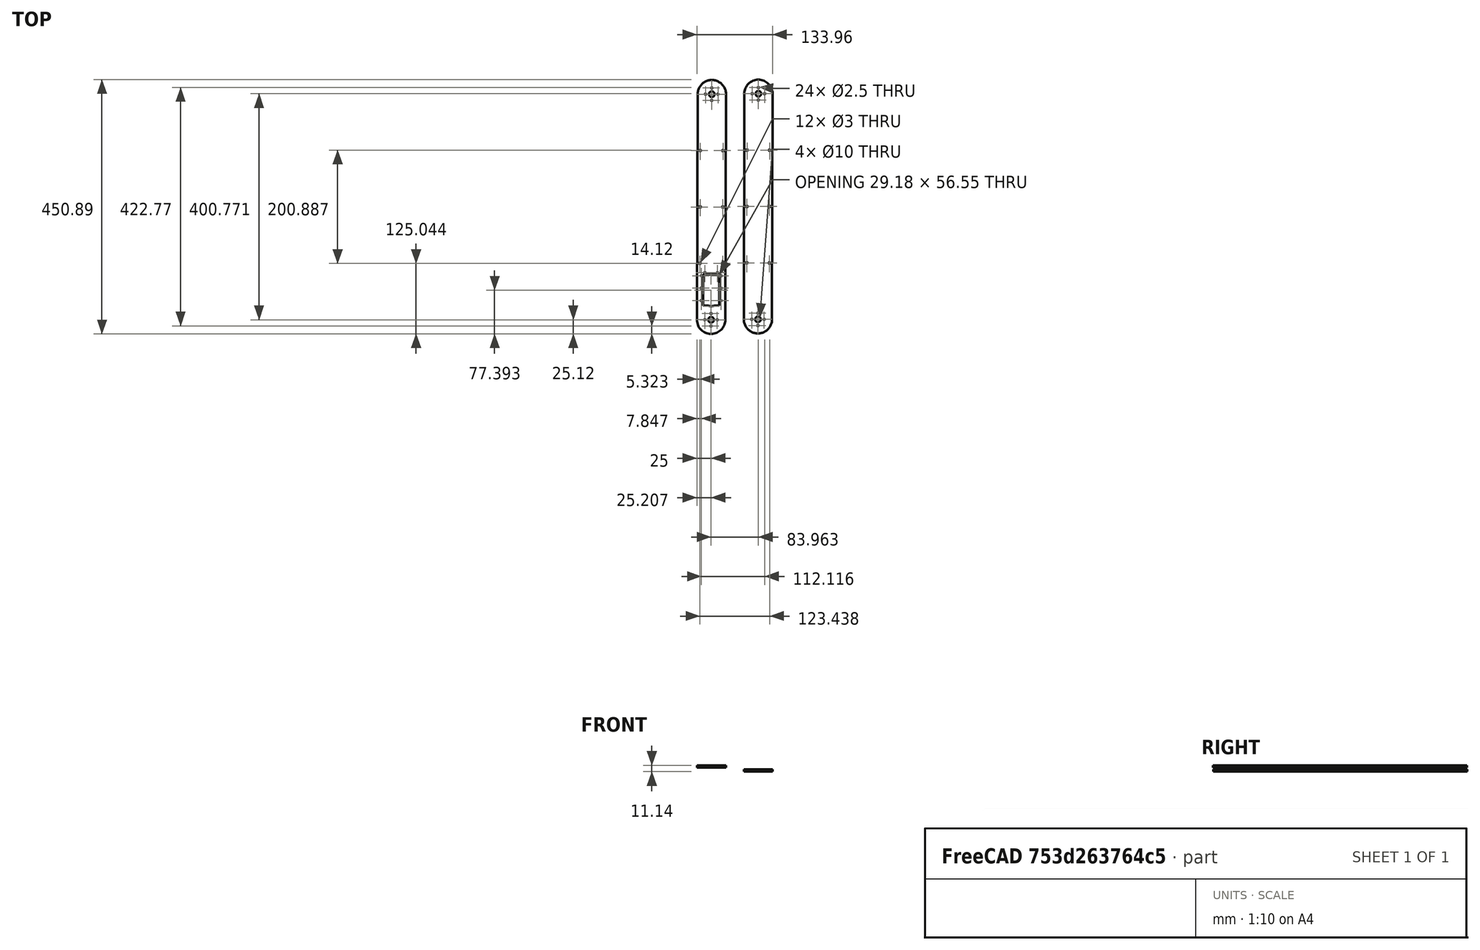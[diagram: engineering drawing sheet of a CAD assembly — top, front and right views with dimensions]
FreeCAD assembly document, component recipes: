
FREECAD ASSEMBLY — COMPONENT RECIPES ("arm_assembly2")

This assembly document has 4 components, labeled P0..P3 below (a component is one placed body or linked part). 2 of them carry a construction recipe — the FreeCAD feature program that regenerates the part from scratch, quoted from this document or its linked companion documents; the rest are supplied as boundary geometry only. No exploded tour is included for this assembly.
COMPONENT P0 — recipe-attached ("arm_low_1", modeled in this document).
Construction recipe (the document's own serialized feature program — sketch geometry with constraints, then the solid features built on it; lengths are millimeters unless a unit is written):

FEATURE [Sketcher::SketchObject] Sketch
  ArcFitTolerance = 1e-06
  AttachmentSupport = -> [XY_Plane]
  FullyConstrained = false
  MakeInternals = false
  MapMode = 5
  sketch-geometry (67):
    g0: LineSegment [constr] StartX=1.5008e-12 StartY=20 StartZ=0 EndX=1.5008e-12 EndY=-20 EndZ=0
    g1: LineSegment [constr] StartX=-2.359e-12 StartY=0 StartZ=0 EndX=-2.359e-12 EndY=400 EndZ=0
    g2: LineSegment [constr] StartX=1.5008e-12 StartY=20 StartZ=0 EndX=1.5008e-12 EndY=25 EndZ=0
    g3: Circle CenterX=-2.359e-12 CenterY=400 CenterZ=0 NormalX=0 NormalY=0 NormalZ=1 AngleXU=0 Radius=5
    g4: Circle CenterX=-2.359e-12 CenterY=400 CenterZ=0 NormalX=0 NormalY=0 NormalZ=1 AngleXU=0 Radius=2
    g5: Circle CenterX=-10.9997 CenterY=400 CenterZ=0 NormalX=0 NormalY=0 NormalZ=1 AngleXU=0 Radius=1.25
    g6: Circle CenterX=0 CenterY=389 CenterZ=0 NormalX=0 NormalY=0 NormalZ=1 AngleXU=0 Radius=1.25
    g7: Circle CenterX=10.9997 CenterY=400 CenterZ=0 NormalX=0 NormalY=0 NormalZ=1 AngleXU=0 Radius=1.25
    g8: Circle CenterX=0 CenterY=411 CenterZ=0 NormalX=0 NormalY=0 NormalZ=1 AngleXU=0 Radius=1.25
    g9: LineSegment [constr] StartX=0 StartY=-5 StartZ=0 EndX=0 EndY=5.99996 EndZ=0
    g10: Circle [constr] CenterX=0 CenterY=0 CenterZ=0 NormalX=0 NormalY=0 NormalZ=1 AngleXU=0 Radius=14
    g11: LineSegment [constr] StartX=0 StartY=0 StartZ=0 EndX=25.23 EndY=0 EndZ=0
    g12: Circle [constr] CenterX=0 CenterY=-3.8e-05 CenterZ=0 NormalX=0 NormalY=0 NormalZ=1 AngleXU=0 Radius=11
    g13: Circle CenterX=0 CenterY=0 CenterZ=0 NormalX=0 NormalY=0 NormalZ=1 AngleXU=0 Radius=5
    g14: Circle CenterX=10.9997 CenterY=0 CenterZ=0 NormalX=0 NormalY=0 NormalZ=1 AngleXU=0 Radius=1.25
    g15: Circle CenterX=-10.9997 CenterY=0 CenterZ=0 NormalX=0 NormalY=0 NormalZ=1 AngleXU=0 Radius=1.25
    g16: Circle CenterX=0 CenterY=-10.9997 CenterZ=0 NormalX=0 NormalY=0 NormalZ=1 AngleXU=0 Radius=1.25
    g17: Circle CenterX=0 CenterY=11 CenterZ=0 NormalX=0 NormalY=0 NormalZ=1 AngleXU=0 Radius=1.25
    g18: LineSegment [constr] StartX=0 StartY=0 StartZ=0 EndX=-25 EndY=0 EndZ=0
    g19: LineSegment [constr] StartX=20.1368 StartY=86.0999 StartZ=0 EndX=20.1368 EndY=24.9999 EndZ=0
    g20: LineSegment [constr] StartX=0.036848 StartY=80.5 StartZ=0 EndX=14.5368 EndY=80.5 EndZ=0
    g21: LineSegment StartX=14.5368 StartY=80.5 StartZ=0 EndX=-14.4632 EndY=80.5 EndZ=0
    g22: LineSegment StartX=14.5368 StartY=80.5 StartZ=0 EndX=14.5368 EndY=24.9999 EndZ=0
    g23: Circle CenterX=11.0368 CenterY=83.3 CenterZ=0 NormalX=0 NormalY=0 NormalZ=1 AngleXU=0 Radius=1.25
    g24: Circle CenterX=17.3368 CenterY=78 CenterZ=0 NormalX=0 NormalY=0 NormalZ=1 AngleXU=0 Radius=1.25
    g25: LineSegment [constr] StartX=-20.0632 StartY=86.0999 StartZ=0 EndX=20.1368 EndY=86.0999 EndZ=0
    g26: Circle CenterX=17.3368 CenterY=56 CenterZ=0 NormalX=0 NormalY=0 NormalZ=1 AngleXU=0 Radius=1.25
    g27: Circle CenterX=17.3368 CenterY=34 CenterZ=0 NormalX=0 NormalY=0 NormalZ=1 AngleXU=0 Radius=1.25
    g28: Circle [constr] CenterX=0.036848 CenterY=37.9999 CenterZ=0 NormalX=0 NormalY=0 NormalZ=1 AngleXU=0 Radius=14
    g29: ArcOfCircle CenterX=0.036848 CenterY=37.9999 CenterZ=0 NormalX=0 NormalY=0 NormalZ=1 AngleXU=0 Radius=14 StartAngle=4.33214 EndAngle=5.09264
    g30: LineSegment StartX=5.233 StartY=24.9999 StartZ=0 EndX=14.5368 EndY=24.9999 EndZ=0
    g31: LineSegment [constr] StartX=14.5368 StartY=24.9999 StartZ=0 EndX=20.1368 EndY=24.9999 EndZ=0
    g32: LineSegment [constr] StartX=17.3368 StartY=56 StartZ=0 EndX=-17.2632 EndY=56 EndZ=0
    g33: LineSegment [constr] StartX=-20.0632 StartY=24.9999 StartZ=0 EndX=-20.0632 EndY=86.0999 EndZ=0
    g34: LineSegment StartX=-14.4632 StartY=80.5 StartZ=0 EndX=-14.4632 EndY=24.9999 EndZ=0
    g35: Circle CenterX=-17.2632 CenterY=78 CenterZ=0 NormalX=0 NormalY=0 NormalZ=1 AngleXU=0 Radius=1.25
    g36: Circle CenterX=-10.9632 CenterY=83.3 CenterZ=0 NormalX=0 NormalY=0 NormalZ=1 AngleXU=0 Radius=1.25
    g37: Circle CenterX=-17.2632 CenterY=56 CenterZ=0 NormalX=0 NormalY=0 NormalZ=1 AngleXU=0 Radius=1.25
    g38: Circle CenterX=-17.2632 CenterY=34 CenterZ=0 NormalX=0 NormalY=0 NormalZ=1 AngleXU=0 Radius=1.25
    g39: LineSegment StartX=-14.4632 StartY=24.9999 StartZ=0 EndX=-5.15931 EndY=24.9999 EndZ=0
    g40: LineSegment [constr] StartX=-20.0632 StartY=24.9999 StartZ=0 EndX=-14.4632 EndY=24.9999 EndZ=0
    g41: ArcOfCircle CenterX=0.115002 CenterY=3.75548e-06 CenterZ=0 NormalX=0 NormalY=0 NormalZ=1 AngleXU=0 Radius=25.115 StartAngle=3.14159 EndAngle=6.28319
    g42: ArcOfCircle CenterX=0.115002 CenterY=399.959 CenterZ=0 NormalX=0 NormalY=0 NormalZ=1 AngleXU=0 Radius=25.115 StartAngle=0 EndAngle=3.14159
    g43: LineSegment StartX=-25 StartY=3.75548e-06 StartZ=0 EndX=-25 EndY=399.959 EndZ=0
    g44: LineSegment StartX=25.23 StartY=3.75548e-06 StartZ=0 EndX=25.23 EndY=399.959 EndZ=0
    g45: LineSegment [constr] StartX=25.23 StartY=199.98 StartZ=0 EndX=-25 EndY=199.98 EndZ=0
    g46: LineSegment [constr] StartX=25.23 StartY=199.98 StartZ=0 EndX=55.23 EndY=199.98 EndZ=0
    g47: LineSegment [constr] StartX=25.23 StartY=0 StartZ=0 EndX=55.23 EndY=0 EndZ=0
    g48: LineSegment [constr] StartX=55.23 StartY=0 StartZ=0 EndX=55.23 EndY=199.98 EndZ=0
    g49: LineSegment [constr] StartX=55.23 StartY=99.9898 StartZ=0 EndX=25.23 EndY=99.9898 EndZ=0
    g50: LineSegment [constr] StartX=25.23 StartY=99.9898 StartZ=0 EndX=-25 EndY=99.9898 EndZ=0
    g51: LineSegment [constr] StartX=25.23 StartY=399.959 StartZ=0 EndX=55.23 EndY=399.959 EndZ=0
    g52: LineSegment [constr] StartX=55.23 StartY=399.959 StartZ=0 EndX=55.23 EndY=199.98 EndZ=0
    g53: LineSegment [constr] StartX=55.23 StartY=299.969 StartZ=0 EndX=25.23 EndY=299.969 EndZ=0
    g54: LineSegment [constr] StartX=25.23 StartY=299.969 StartZ=0 EndX=-25 EndY=299.969 EndZ=0
    g55: LineSegment [constr] StartX=-25 StartY=299.969 StartZ=0 EndX=-20 EndY=299.969 EndZ=0
    g56: LineSegment [constr] StartX=-20 StartY=299.969 StartZ=0 EndX=-20 EndY=199.98 EndZ=0
    g57: LineSegment [constr] StartX=-20 StartY=199.98 StartZ=0 EndX=-20 EndY=99.9898 EndZ=0
    g58: LineSegment [constr] StartX=25.23 StartY=299.969 StartZ=0 EndX=20.23 EndY=299.969 EndZ=0
    g59: LineSegment [constr] StartX=20.23 StartY=299.969 StartZ=0 EndX=20.23 EndY=199.98 EndZ=0
    g60: LineSegment [constr] StartX=20.23 StartY=199.98 StartZ=0 EndX=20.23 EndY=99.9898 EndZ=0
    g61: Circle CenterX=-20 CenterY=299.969 CenterZ=0 NormalX=0 NormalY=0 NormalZ=1 AngleXU=0 Radius=1.5
    g62: Circle CenterX=20.23 CenterY=299.969 CenterZ=0 NormalX=0 NormalY=0 NormalZ=1 AngleXU=0 Radius=1.5
    g63: Circle CenterX=-20 CenterY=199.98 CenterZ=0 NormalX=0 NormalY=0 NormalZ=1 AngleXU=0 Radius=1.5
    g64: Circle CenterX=20.23 CenterY=199.98 CenterZ=0 NormalX=0 NormalY=0 NormalZ=1 AngleXU=0 Radius=1.5
    g65: Circle CenterX=-20 CenterY=99.9898 CenterZ=0 NormalX=0 NormalY=0 NormalZ=1 AngleXU=0 Radius=1.5
    g66: Circle CenterX=20.23 CenterY=99.9898 CenterZ=0 NormalX=0 NormalY=0 NormalZ=1 AngleXU=0 Radius=1.5
  constraints (132):
    c: Vertical(g0)
    c: Vertical(g1)
    c: Coincident(g2,g0)
    c: Vertical(g2)
    c: Diameter(g3) = 10
    c: Coincident(g3,g1)
    c: Diameter(g4) = 4
    c: Coincident(g4,g1)
    c: Diameter(g8) = 2.5
    c: Diameter(g5) = 2.5
    c: Diameter(g6) = 2.5
    c: Diameter(g7) = 2.5
    c: Vertical(g9)
    c: Diameter(g10) = 28
    c: Coincident(g18,g10)
    c: Horizontal(g18)
    c: Coincident(g11,g10)
    c: Horizontal(g11)
    c: Diameter(g12) = 22
    c: Diameter(g13) = 10
    c: Coincident(g13,g10)
    c: Diameter(g17) = 2.5
    c: Diameter(g15) = 2.5
    c: Diameter(g16) = 2.5
    c: Diameter(g14) = 2.5
    c: Coincident(g25,g19)
    c: Coincident(g33,g25)
    c: Horizontal(g25)
    c: Vertical(g19)
    c: Vertical(g33)
    c: Distance(g19,g33) = 40.2
    c: Distance(g25,g33) = 61.1
    c: Diameter(g29) = 28
    c: Horizontal(g20)
    c: Coincident(g21,g20)
    c: Horizontal(g21)
    c: Coincident(g34,g21)
    c: Vertical(g34)
    c: Coincident(g22,g20)
    c: Vertical(g22)
    c: Diameter(g23) = 2.5
    c: Equal(g23,g36)
    c: Equal(g23,g27)
    c: Equal(g23,g38)
    c: Equal(g23,g37)
    c: Equal(g23,g35)
    c: Equal(g23,g24)
    c: Equal(g23,g26)
    c: Coincident(g28,g29)
    c: PointOnObject(g29,g28)
    c: Coincident(g30,g29)
    c: Coincident(g30,g22)
    c: Horizontal(g30)
    c: Coincident(g31,g22)
    c: Coincident(g31,g19)
    c: Horizontal(g31)
    c: Coincident(g39,g34)
    c: Coincident(g39,g29)
    c: Horizontal(g39)
    c: Coincident(g40,g33)
    c: Coincident(g40,g34)
    c: Horizontal(g40)
    c: Coincident(g32,g26)
    c: Coincident(g32,g37)
    c: Horizontal(g32)
    c: DistanceY(g28,g1) = 362
    c: Tangent(g41,g43) = 1.5708
    c: Tangent(g41,g44) = -1.5708
    c: Tangent(g42,g43) = 1.5708
    c: Tangent(g42,g44) = -1.5708
    c: Equal(g41,g42)
    c: Symmetric(g44,g44,g45)
    c: Symmetric(g43,g43,g45)
    c: Horizontal(g45)
    c: Distance(g46) = 30
    c: Horizontal(g46)
    c: Coincident(g46,g45)
    c: Distance(g47) = 30
    c: Horizontal(g47)
    c: Coincident(g47,g11)
    c: PointOnObject(g47,g-1)
    c: Coincident(g48,g47)
    c: Coincident(g48,g46)
    c: Vertical(g48)
    c: Symmetric(g48,g48,g49)
    c: PointOnObject(g49,g44)
    c: Horizontal(g49)
    c: Coincident(g50,g49)
    c: PointOnObject(g50,g43)
    c: Horizontal(g50)
    c: Distance(g51) = 30
    c: Horizontal(g51)
    c: Coincident(g51,g42)
    c: Coincident(g52,g51)
    c: Coincident(g52,g46)
    c: Symmetric(g52,g52,g53)
    c: PointOnObject(g53,g44)
    c: Horizontal(g53)
    c: Coincident(g54,g53)
    c: PointOnObject(g54,g43)
    c: Horizontal(g54)
    c: Distance(g55) = 5
    c: Coincident(g55,g54)
    c: PointOnObject(g55,g54)
    c: Coincident(g56,g55)
    c: PointOnObject(g56,g45)
    c: Vertical(g56)
    c: Coincident(g57,g56)
    c: PointOnObject(g57,g50)
    c: Vertical(g57)
    c: Distance(g58) = 5
    c: Coincident(g58,g53)
    c: PointOnObject(g58,g54)
    c: Coincident(g59,g58)
    c: PointOnObject(g59,g45)
    c: Vertical(g59)
    c: Coincident(g60,g59)
    c: PointOnObject(g60,g50)
    c: Vertical(g60)
    c: Coincident(g61,g55)
    c: Diameter(g61) = 3
    c: Coincident(g62,g58)
    c: Equal(g61,g62)
    c: Coincident(g63,g56)
    c: Equal(g61,g63)
    c: Coincident(g64,g59)
    c: Equal(g63,g64)
    c: Coincident(g65,g57)
    c: Equal(g63,g65)
    c: Coincident(g66,g60)
    c: Equal(g65,g66)
    c: DistanceY(g41,g28) = 37.9999
FEATURE [PartDesign::Pad] Pad
  Direction = (0,0,1)
  Length = 4
  Length2 = 10
  Profile = -> Sketch
  ReferenceAxis = -> Sketch [N_Axis]
  Refine = true
  Suppressed = false
  Type = 0
FEATURE [PartDesign::Body] Body  label="arm_low_1"
  AllowCompound = false
  Group = -> [Sketch,Pad]
  Origin = -> Origin
  Placement = pos=(0,0,25.3) rot=(0,0,-1;0.003227rad)
  Tip = -> Pad
COMPONENT P1 — recipe-attached ("arm_high_1", modeled in this document).
Construction recipe (the document's own serialized feature program — sketch geometry with constraints, then the solid features built on it; lengths are millimeters unless a unit is written):

FEATURE [Sketcher::SketchObject] Sketch001
  ArcFitTolerance = 1e-06
  FullyConstrained = false
  MakeInternals = false
  MapMode = 5
  sketch-geometry (41):
    g0: Circle [constr] CenterX=7e-16 CenterY=0.000303 CenterZ=0 NormalX=0 NormalY=0 NormalZ=1 AngleXU=0 Radius=14
    g1: LineSegment [constr] StartX=7e-16 StartY=0.000303 StartZ=0 EndX=7e-16 EndY=400.001 EndZ=0
    g2: Circle CenterX=7e-16 CenterY=400.001 CenterZ=0 NormalX=0 NormalY=0 NormalZ=1 AngleXU=0 Radius=5
    g3: Circle CenterX=7e-16 CenterY=0 CenterZ=0 NormalX=0 NormalY=0 NormalZ=1 AngleXU=0 Radius=5
    g4: Circle CenterX=7e-16 CenterY=400.001 CenterZ=0 NormalX=0 NormalY=0 NormalZ=1 AngleXU=0 Radius=2
    g5: Circle CenterX=7e-16 CenterY=0.000303 CenterZ=0 NormalX=0 NormalY=0 NormalZ=1 AngleXU=0 Radius=2
    g6: Circle [constr] CenterX=0 CenterY=0 CenterZ=0 NormalX=0 NormalY=0 NormalZ=1 AngleXU=0 Radius=11
    g7: ArcOfCircle CenterX=7e-16 CenterY=0 CenterZ=0 NormalX=0 NormalY=0 NormalZ=1 AngleXU=0 Radius=25 StartAngle=3.14159 EndAngle=6.28319
    g8: ArcOfCircle CenterX=7e-16 CenterY=400.001 CenterZ=0 NormalX=0 NormalY=0 NormalZ=1 AngleXU=0 Radius=25 StartAngle=6e-16 EndAngle=3.14159
    g9: LineSegment StartX=-25 StartY=-8e-15 StartZ=0 EndX=-25 EndY=400.001 EndZ=0
    g10: LineSegment StartX=25 StartY=0 StartZ=0 EndX=25 EndY=400.001 EndZ=0
    g11: Circle CenterX=10.9997 CenterY=400.001 CenterZ=0 NormalX=0 NormalY=0 NormalZ=1 AngleXU=0 Radius=1.25
    g12: Circle CenterX=0 CenterY=411.001 CenterZ=0 NormalX=0 NormalY=0 NormalZ=1 AngleXU=0 Radius=1.25
    g13: Circle CenterX=-10.9997 CenterY=400.001 CenterZ=0 NormalX=0 NormalY=0 NormalZ=1 AngleXU=0 Radius=1.25
    g14: Circle CenterX=0 CenterY=389.001 CenterZ=0 NormalX=0 NormalY=0 NormalZ=1 AngleXU=0 Radius=1.25
    g15: Circle CenterX=10.9997 CenterY=0.000303 CenterZ=0 NormalX=0 NormalY=0 NormalZ=1 AngleXU=0 Radius=1.25
    g16: Circle CenterX=0 CenterY=11 CenterZ=0 NormalX=0 NormalY=0 NormalZ=1 AngleXU=0 Radius=1.25
    g17: Circle CenterX=-10.9997 CenterY=0.000303 CenterZ=0 NormalX=0 NormalY=0 NormalZ=1 AngleXU=0 Radius=1.25
    g18: Circle CenterX=0 CenterY=-10.9994 CenterZ=0 NormalX=0 NormalY=0 NormalZ=1 AngleXU=0 Radius=1.25
    g19: LineSegment [constr] StartX=25 StartY=200 StartZ=0 EndX=-25 EndY=200 EndZ=0
    g20: LineSegment [constr] StartX=25 StartY=200 StartZ=0 EndX=55 EndY=200 EndZ=0
    g21: LineSegment [constr] StartX=25 StartY=0 StartZ=0 EndX=55 EndY=0 EndZ=0
    g22: LineSegment [constr] StartX=25 StartY=400.001 StartZ=0 EndX=55 EndY=400.001 EndZ=0
    g23: LineSegment [constr] StartX=55 StartY=200 StartZ=0 EndX=55 EndY=400.001 EndZ=0
    g24: LineSegment [constr] StartX=55 StartY=200 StartZ=0 EndX=55 EndY=0 EndZ=0
    g25: LineSegment [constr] StartX=55 StartY=100 StartZ=0 EndX=25 EndY=100 EndZ=0
    g26: LineSegment [constr] StartX=25 StartY=100 StartZ=0 EndX=-25 EndY=100 EndZ=0
    g27: LineSegment [constr] StartX=55 StartY=300 StartZ=0 EndX=25 EndY=300 EndZ=0
    g28: LineSegment [constr] StartX=25 StartY=300 StartZ=0 EndX=-25 EndY=300 EndZ=0
    g29: LineSegment [constr] StartX=-25 StartY=300 StartZ=0 EndX=-20 EndY=300 EndZ=0
    g30: LineSegment [constr] StartX=-20 StartY=300 StartZ=0 EndX=-20 EndY=200 EndZ=0
    g31: LineSegment [constr] StartX=-20 StartY=200 StartZ=0 EndX=-20 EndY=100 EndZ=0
    g32: LineSegment [constr] StartX=25 StartY=100 StartZ=0 EndX=20 EndY=100 EndZ=0
    g33: LineSegment [constr] StartX=20 StartY=100 StartZ=0 EndX=20 EndY=200 EndZ=0
    g34: LineSegment [constr] StartX=20 StartY=200 StartZ=0 EndX=20 EndY=300 EndZ=0
    g35: Circle CenterX=-20 CenterY=300 CenterZ=0 NormalX=0 NormalY=0 NormalZ=1 AngleXU=0 Radius=1.5
    g36: Circle CenterX=20 CenterY=300 CenterZ=0 NormalX=0 NormalY=0 NormalZ=1 AngleXU=0 Radius=1.5
    g37: Circle CenterX=-20 CenterY=200 CenterZ=0 NormalX=0 NormalY=0 NormalZ=1 AngleXU=0 Radius=1.5
    g38: Circle CenterX=20 CenterY=200 CenterZ=0 NormalX=0 NormalY=0 NormalZ=1 AngleXU=0 Radius=1.5
    g39: Circle CenterX=-20 CenterY=100 CenterZ=0 NormalX=0 NormalY=0 NormalZ=1 AngleXU=0 Radius=1.5
    g40: Circle CenterX=20 CenterY=100 CenterZ=0 NormalX=0 NormalY=0 NormalZ=1 AngleXU=0 Radius=1.5
  constraints (85):
    c: Diameter(g0) = 28
    c: Coincident(g1,g0)
    c: Vertical(g1)
    c: Coincident(g2,g1)
    c: Diameter(g3) = 10
    c: Diameter(g4) = 4
    c: Coincident(g4,g1)
    c: Diameter(g5) = 4
    c: Coincident(g5,g0)
    c: Diameter(g6) = 22
    c: Tangent(g7,g9) = 1.5708
    c: Tangent(g7,g10) = -1.5708
    c: Tangent(g8,g9) = 1.5708
    c: Tangent(g8,g10) = -1.5708
    c: Equal(g7,g8)
    c: Radius(g7) = 25
    c: Coincident(g7,g3)
    c: Coincident(g8,g1)
    c: Vertical(g9)
    c: Diameter(g12) = 2.5
    c: Diameter(g13) = 2.5
    c: Diameter(g14) = 2.5
    c: Diameter(g11) = 2.5
    c: Diameter(g16) = 2.5
    c: Diameter(g17) = 2.5
    c: Diameter(g18) = 2.5
    c: Diameter(g15) = 2.5
    c: Symmetric(g10,g10,g19)
    c: Symmetric(g9,g9,g19)
    c: Distance(g20) = 30
    c: Horizontal(g20)
    c: Coincident(g20,g19)
    c: Distance(g21) = 30
    c: Horizontal(g21)
    c: Coincident(g21,g7)
    c: PointOnObject(g21,g-1)
    c: Distance(g22) = 30
    c: Horizontal(g22)
    c: Coincident(g22,g8)
    c: Coincident(g23,g20)
    c: Coincident(g23,g22)
    c: Coincident(g24,g20)
    c: Coincident(g24,g21)
    c: Symmetric(g24,g24,g25)
    c: PointOnObject(g25,g10)
    c: Horizontal(g25)
    c: Coincident(g26,g25)
    c: PointOnObject(g26,g9)
    c: Horizontal(g26)
    c: Symmetric(g23,g23,g27)
    c: PointOnObject(g27,g10)
    c: Horizontal(g27)
    c: Coincident(g28,g27)
    c: PointOnObject(g28,g9)
    c: Horizontal(g28)
    c: Distance(g29) = 5
    c: Horizontal(g29)
    c: Coincident(g29,g28)
    c: Coincident(g30,g29)
    c: PointOnObject(g30,g19)
    c: Vertical(g30)
    c: Coincident(g31,g30)
    c: PointOnObject(g31,g26)
    c: Vertical(g31)
    c: Distance(g32) = 5
    c: Horizontal(g32)
    c: Coincident(g32,g25)
    c: Coincident(g33,g32)
    c: PointOnObject(g33,g19)
    c: Vertical(g33)
    c: Coincident(g34,g33)
    c: PointOnObject(g34,g28)
    c: Vertical(g34)
    c: Diameter(g35) = 3
    c: Coincident(g35,g29)
    c: Coincident(g36,g34)
    c: Equal(g35,g36)
    c: Coincident(g37,g30)
    c: Equal(g35,g37)
    c: Coincident(g38,g33)
    c: Equal(g37,g38)
    c: Coincident(g39,g31)
    c: Equal(g37,g39)
    c: Coincident(g40,g32)
    c: Equal(g39,g40)
FEATURE [PartDesign::Pad] Pad001
  Direction = (0,0,1)
  Length = 4
  Length2 = 10
  Profile = -> Sketch001
  ReferenceAxis = -> Sketch001 [N_Axis]
  Refine = true
  Suppressed = false
  Type = 0
FEATURE [PartDesign::Body] Body001  label="arm_high_1"
  AllowCompound = false
  Group = -> [Sketch001,Pad001]
  Origin = -> Origin001
  Placement = pos=(83.1539,0.770773,18.1622) rot=(0,0,-1;0.002023rad)
  Tip = -> Pad001
COMPONENT P2 — geometry summary ("DC05_M01_DUMMY"; no construction recipe available for this part):
  bounding box: 62.1 x 50.0 x 40.2 mm
  tessellated surface: 23,948 triangles
  volume: 72104 mm^3 (58% of its bounding box)
  symmetry: mirror-symmetric across its x mid-plane
COMPONENT P3 — geometry summary ("DC05_M01_DUMMY001"; no construction recipe available for this part):
  bounding box: 62.1 x 50.0 x 40.3 mm
  tessellated surface: 23,948 triangles
  volume: 72104 mm^3 (58% of its bounding box)
  symmetry: mirror-symmetric across its x mid-plane
PROVENANCE & LICENSES
A FreeCAD (.FCStd) document from a public repository crawl; recipes are the document's own serialized feature recipes (and, for linked parts, companion documents' recipes).
License: unknown-license-file.
